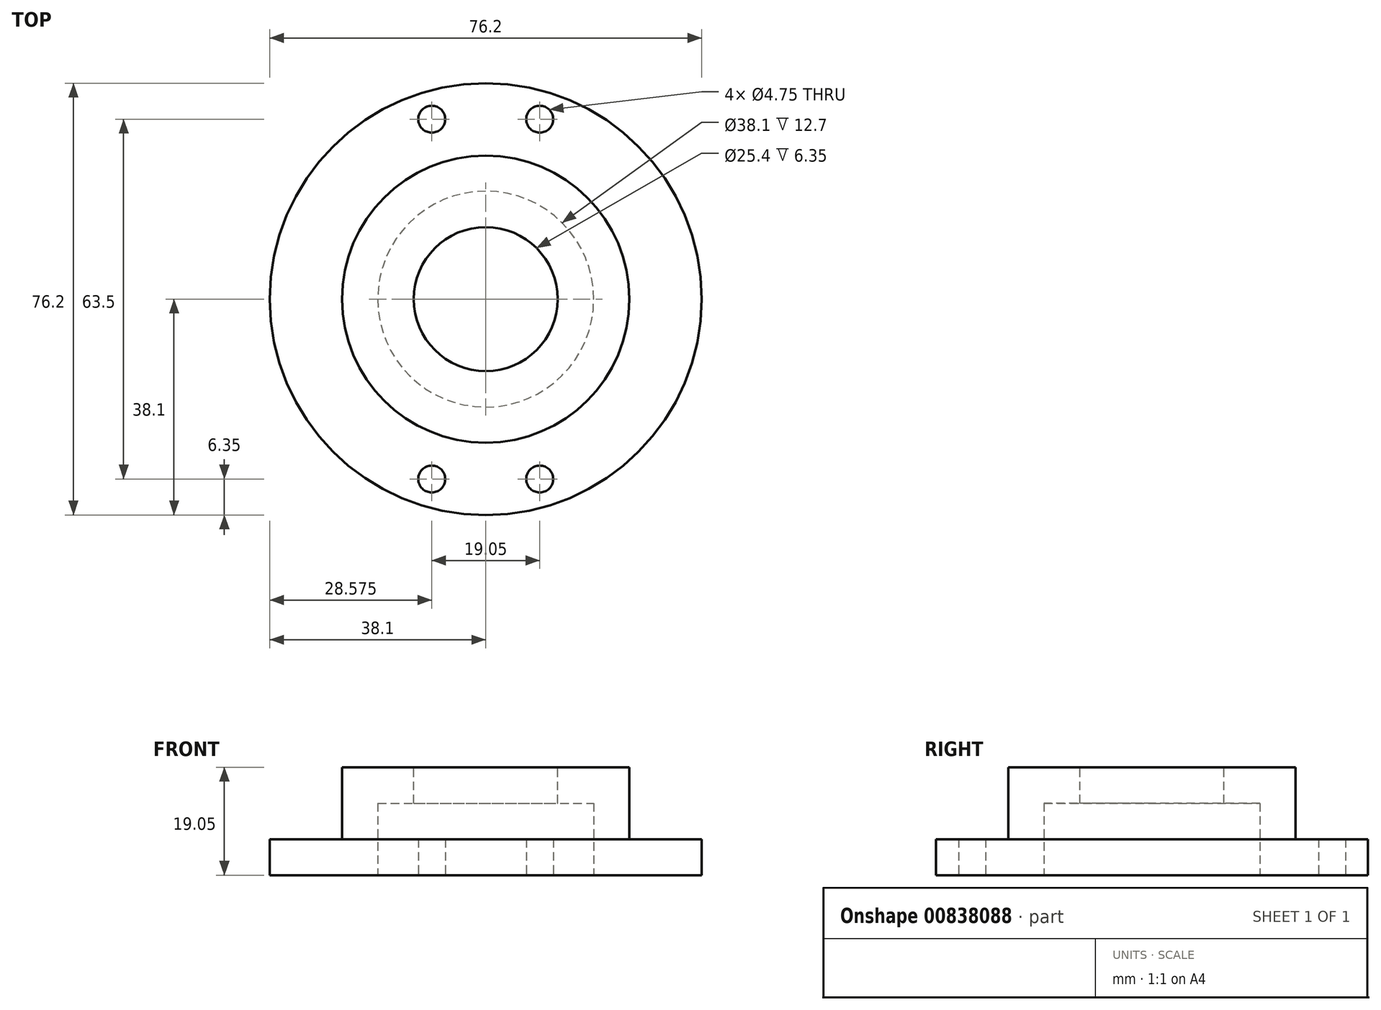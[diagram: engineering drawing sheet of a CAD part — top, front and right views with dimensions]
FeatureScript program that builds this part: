
annotation { "Feature Type Name" : "Feature", "Feature Type Description" : "" }
export const myFeature = defineFeature(function(context is Context, id is Id, definition is map)
    precondition{}
    {
        {
            var Q0;
            Q0=qCreatedBy(makeId("Top.planeOp"),FACE);
            var sketch = newSketch(context, id + "F0", { "sketchPlane" : qUnion([Q0])});
            skCircle(sketch, "E0", {"center": v(0, 0) * mm, "radius": 38.1 * mm});
            skLineSegment(sketch, "E1", {"start": v(0, 0) * mm, "end": v(0, 31.75) * mm, "construction": true});
            skLineSegment(sketch, "E2", {"start": v(0, 31.75) * mm, "end": v(9.53, 31.75) * mm, "construction": true});
            skLineSegment(sketch, "E3", {"start": v(0, 31.75) * mm, "end": v(-9.53, 31.75) * mm, "construction": true});
            skLineSegment(sketch, "E4.MirrorCS", {"start": v(0, 0) * mm, "end": v(0, -31.75) * mm, "construction": true});
            skLineSegment(sketch, "E5.MirrorCS", {"start": v(0, -31.75) * mm, "end": v(9.53, -31.75) * mm, "construction": true});
            skLineSegment(sketch, "E6.MirrorCS", {"start": v(0, -31.75) * mm, "end": v(-9.53, -31.75) * mm, "construction": true});
            skCircle(sketch, "E7", {"center": v(-9.53, 31.75) * mm, "radius": 2.37 * mm});
            skCircle(sketch, "E8.MirrorC", {"center": v(9.53, 31.75) * mm, "radius": 2.37 * mm});
            skCircle(sketch, "E9.MirrorC", {"center": v(9.53, -31.75) * mm, "radius": 2.37 * mm});
            skCircle(sketch, "E10.MirrorC", {"center": v(-9.53, -31.75) * mm, "radius": 2.37 * mm});
            skCircle(sketch, "E11", {"center": v(0, 0) * mm, "radius": 25.4 * mm});
            skSolve(sketch);
        }
        {
            var Q0;
            Q0=makeQuery(id+"F0.imprint","IMPRINT",FACE,{"disambiguationData":[TD([[makeQuery(id+"F0.imprint","IMPRINT",EDGE,{"derivedFrom":sQuery(id+"F0.wireOp",EDGE,"E0")}),1.0]])]});
            var Q1;
            Q1=makeQuery(id+"F0.imprint","IMPRINT",FACE,{"disambiguationData":[TD([[makeQuery(id+"F0.imprint","IMPRINT",EDGE,{"derivedFrom":sQuery(id+"F0.wireOp",EDGE,"E11")}),1.0]])]});
            extrude(context, id + "F1", {"entities" : qUnion([Q0, Q1]), "depth" : 6.35 * mm, "offsetDistance" : 25.4 * mm});
        }
        {
            var Q0;
            Q0=makeQuery(id+"F1.opExtrude","CAP_FACE",FACE,{"disambiguationData":[OSD([sQuery(id+"F0.wireOp",EDGE,"E0"),sQuery(id+"F0.wireOp",EDGE,"E7"),sQuery(id+"F0.wireOp",EDGE,"E8.MirrorC"),sQuery(id+"F0.wireOp",EDGE,"E9.MirrorC"),sQuery(id+"F0.wireOp",EDGE,"E10.MirrorC")])],"isStart":false});
            var sketch = newSketch(context, id + "F2", { "sketchPlane" : qUnion([Q0])});
            skCircle(sketch, "E12", {"center": v(0, 0) * mm, "radius": 25.34 * mm});
            skSolve(sketch);
        }
        {
            var Q0;
            Q0=makeQuery(id+"F2.imprint","IMPRINT",FACE,{"disambiguationData":[TD([[makeQuery(id+"F2.imprint","IMPRINT",EDGE,{"derivedFrom":sQuery(id+"F2.wireOp",EDGE,"E12")}),1.0]])]});
            extrude(context, id + "F3", {"entities" : qUnion([Q0]), "operationType" : NewBodyOperationType.ADD, "depth" : 12.7 * mm, "offsetDistance" : 25.4 * mm});
        }
        {
            var Q0;
            Q0=makeQuery(id+"F1.opExtrude","CAP_FACE",FACE,{"disambiguationData":[OSD([sQuery(id+"F0.wireOp",EDGE,"E0"),sQuery(id+"F0.wireOp",EDGE,"E7"),sQuery(id+"F0.wireOp",EDGE,"E8.MirrorC"),sQuery(id+"F0.wireOp",EDGE,"E9.MirrorC"),sQuery(id+"F0.wireOp",EDGE,"E10.MirrorC")])],"isStart":true});
            var sketch = newSketch(context, id + "F4", { "sketchPlane" : qUnion([Q0])});
            skCircle(sketch, "E13", {"center": v(0, 0) * mm, "radius": 19.05 * mm});
            skSolve(sketch);
        }
        {
            var Q0;
            Q0=makeQuery(id+"F4.imprint","IMPRINT",FACE,{"disambiguationData":[TD([[makeQuery(id+"F4.imprint","IMPRINT",EDGE,{"derivedFrom":sQuery(id+"F4.wireOp",EDGE,"E13")}),1.0]])]});
            extrude(context, id + "F5", {"entities" : qUnion([Q0]), "operationType" : NewBodyOperationType.REMOVE, "oppositeDirection" : true, "depth" : 12.7 * mm, "offsetDistance" : 25.4 * mm});
        }
        {
            var Q0;
            Q0=makeQuery(id+"F3.opExtrude","CAP_FACE",FACE,{"disambiguationData":[OSD([sQuery(id+"F2.wireOp",EDGE,"E12")])],"isStart":false});
            var sketch = newSketch(context, id + "F6", { "sketchPlane" : qUnion([Q0])});
            skCircle(sketch, "E14", {"center": v(0, 0) * mm, "radius": 12.7 * mm});
            skSolve(sketch);
        }
        {
            var Q0;
            Q0=makeQuery(id+"F6.imprint","IMPRINT",FACE,{"disambiguationData":[TD([[makeQuery(id+"F6.imprint","IMPRINT",EDGE,{"derivedFrom":sQuery(id+"F6.wireOp",EDGE,"E14")}),1.0]])]});
            extrude(context, id + "F7", {"entities" : qUnion([Q0]), "operationType" : NewBodyOperationType.REMOVE, "oppositeDirection" : true, "depth" : 25.4 * mm, "offsetDistance" : 25.4 * mm});
        }
    });
